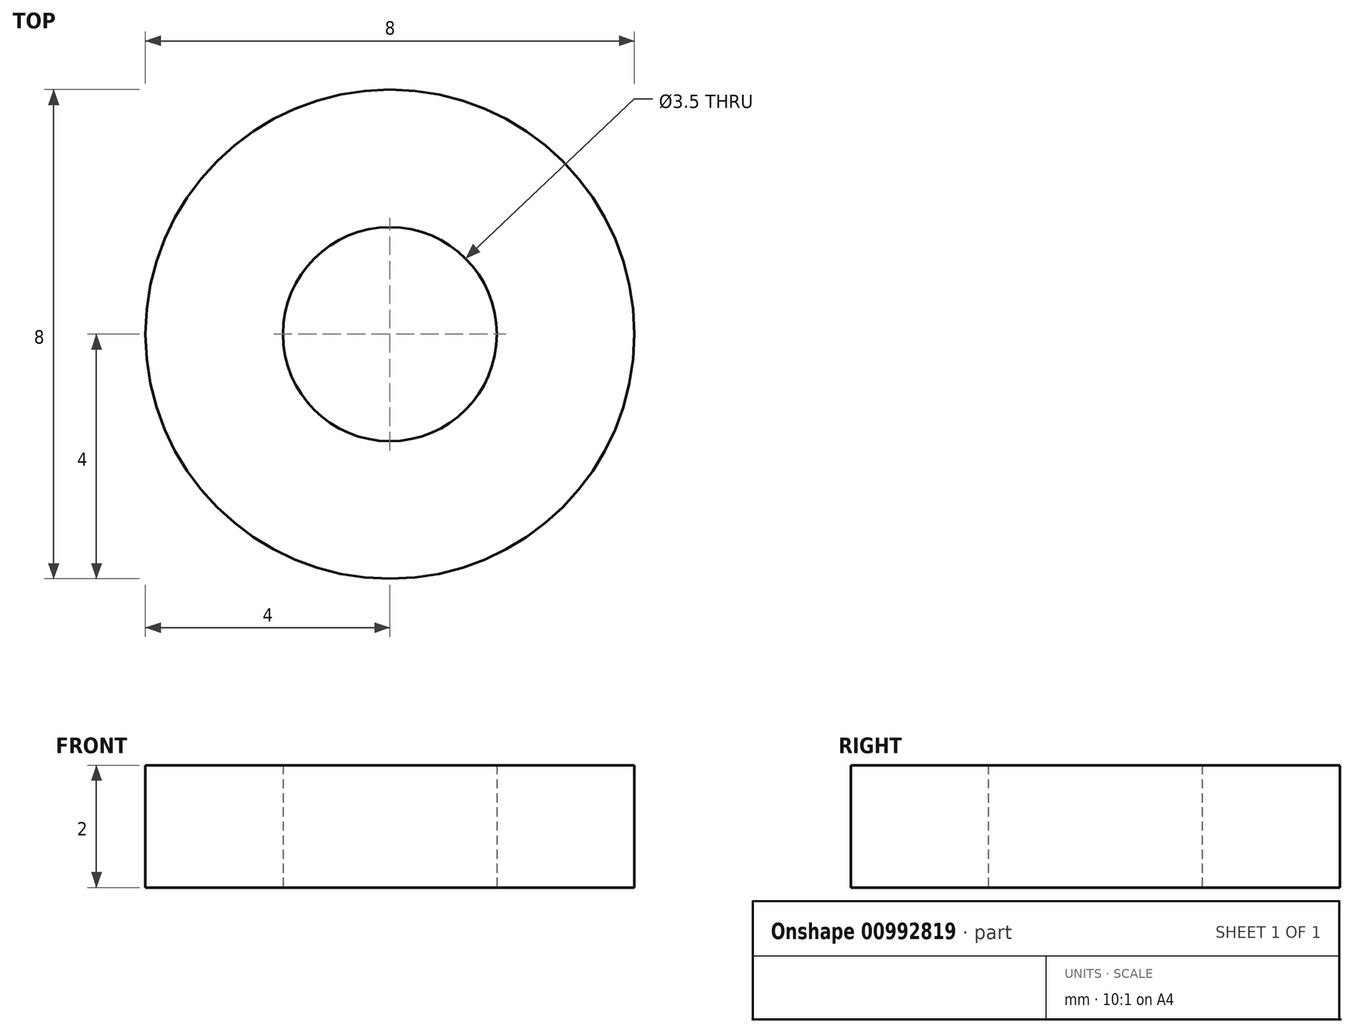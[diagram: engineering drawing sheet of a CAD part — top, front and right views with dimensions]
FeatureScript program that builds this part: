
annotation { "Feature Type Name" : "Feature", "Feature Type Description" : "" }
export const myFeature = defineFeature(function(context is Context, id is Id, definition is map)
    precondition{}
    {
        {
            var Q0;
            Q0=qCreatedBy(makeId("Top.planeOp"),FACE);
            var sketch = newSketch(context, id + "F0", { "sketchPlane" : qUnion([Q0])});
            skCircle(sketch, "E0", {"center": v(0, 0) * mm, "radius": 4 * mm});
            skCircle(sketch, "E1", {"center": v(0, 0) * mm, "radius": 1.75 * mm});
            skSolve(sketch);
        }
        {
            var Q0;
            Q0=makeQuery(id+"F0.imprint","IMPRINT",FACE,{"disambiguationData":[TD([[makeQuery(id+"F0.imprint","IMPRINT",EDGE,{"derivedFrom":sQuery(id+"F0.wireOp",EDGE,"E0")}),1.0]])]});
            extrude(context, id + "F1", {"entities" : qUnion([Q0]), "depth" : 2 * mm, "offsetDistance" : 25 * mm});
        }
    });
